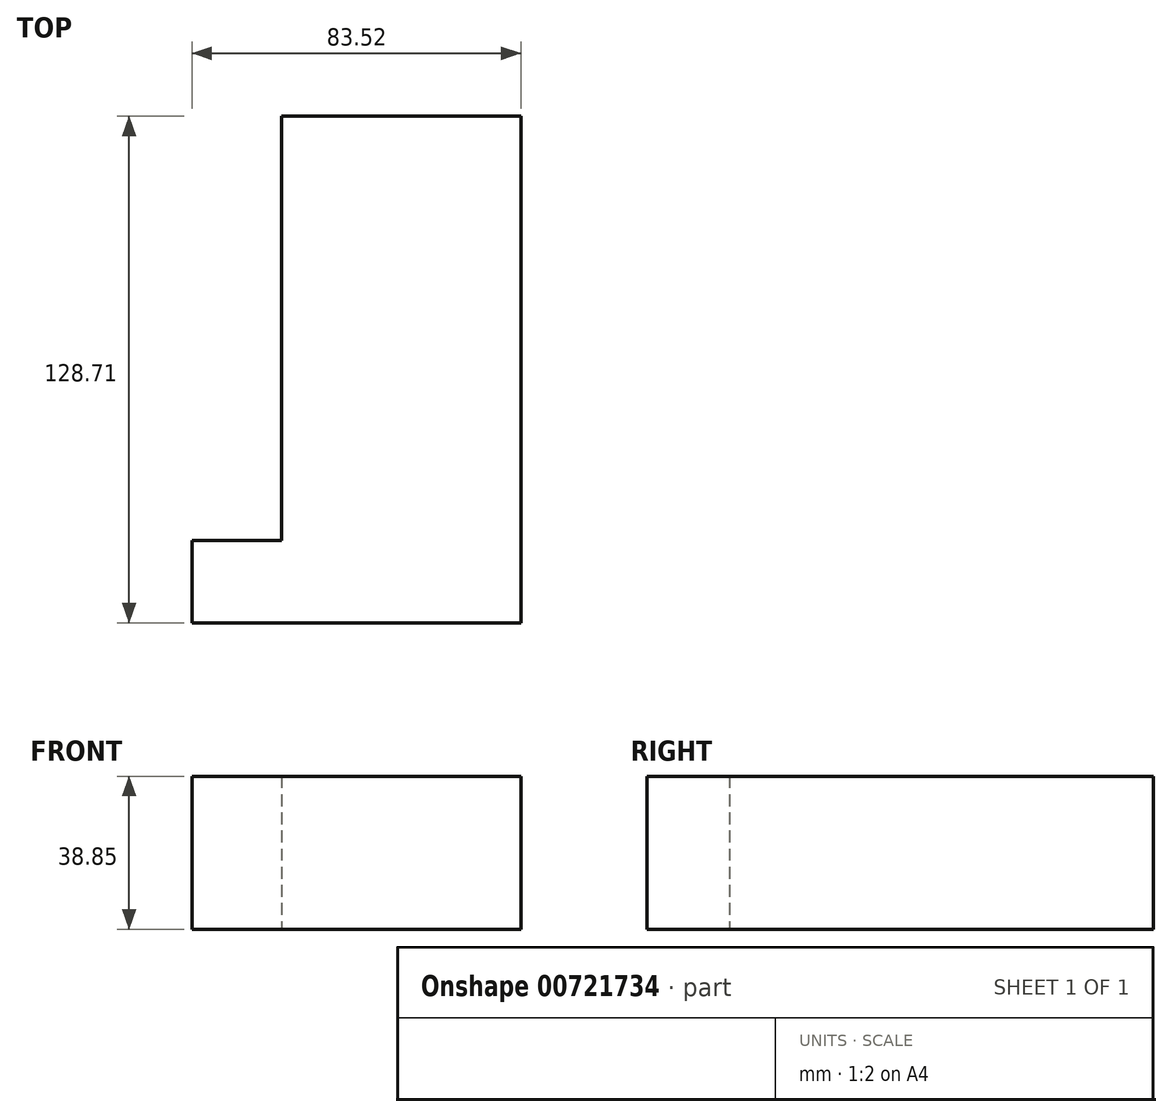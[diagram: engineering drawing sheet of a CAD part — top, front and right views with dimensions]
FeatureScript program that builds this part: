
annotation { "Feature Type Name" : "Feature", "Feature Type Description" : "" }
export const myFeature = defineFeature(function(context is Context, id is Id, definition is map)
    precondition{}
    {
        {
            var Q0;
            Q0=qCreatedBy(makeId("Top.planeOp"),FACE);
            var sketch = newSketch(context, id + "F0", { "sketchPlane" : qUnion([Q0])});
            skLineSegment(sketch, "E0.bottom", {"start": v(-20.99, -41.67) * mm, "end": v(39.74, -41.67) * mm});
            skLineSegment(sketch, "E0.top", {"start": v(-20.99, 66.05) * mm, "end": v(39.74, 66.05) * mm});
            skLineSegment(sketch, "E0.left", {"start": v(-20.99, -41.67) * mm, "end": v(-20.99, 66.05) * mm});
            skLineSegment(sketch, "E0.right", {"start": v(39.74, -41.67) * mm, "end": v(39.74, 66.05) * mm});
            skLineSegment(sketch, "E1.bottom", {"start": v(-43.78, -62.66) * mm, "end": v(-20.99, -62.66) * mm});
            skLineSegment(sketch, "E1.top", {"start": v(-43.78, -41.67) * mm, "end": v(-20.99, -41.67) * mm});
            skLineSegment(sketch, "E1.left", {"start": v(-43.78, -62.66) * mm, "end": v(-43.78, -41.67) * mm});
            skLineSegment(sketch, "E1.right", {"start": v(-20.99, -62.66) * mm, "end": v(-20.99, -41.67) * mm});
            skLineSegment(sketch, "E2.bottom", {"start": v(39.74, -41.67) * mm, "end": v(-43.78, -41.67) * mm});
            skLineSegment(sketch, "E2.top", {"start": v(39.74, -62.66) * mm, "end": v(-43.78, -62.66) * mm});
            skLineSegment(sketch, "E2.left", {"start": v(39.74, -41.67) * mm, "end": v(39.74, -62.66) * mm});
            skLineSegment(sketch, "E2.right", {"start": v(-43.78, -41.67) * mm, "end": v(-43.78, -62.66) * mm});
            skSolve(sketch);
        }
        {
            var Q0;
            {var subQ0=makeQuery(id+"F0.imprint","IMPRINT",EDGE,{"derivedFrom":sQuery(id+"F0.wireOp",EDGE,"E0.bottom")});Q0=qUnion([makeQuery(id+"F0.imprint","IMPRINT",FACE,{"disambiguationData":[TD([[subQ0,1.0]])]}),makeQuery(id+"F0.imprint","IMPRINT",FACE,{"disambiguationData":[TD([[makeQuery(id+"F0.imprint","IMPRINT",EDGE,{"derivedFrom":sQuery(id+"F0.wireOp",EDGE,"E1.bottom")}),1.0]])]}),makeQuery(id+"F0.imprint","IMPRINT",FACE,{"disambiguationData":[TD([[subQ0,-1.0]])]})]);}
            extrude(context, id + "F1", {"entities" : qUnion([Q0]), "depth" : 38.85 * mm, "offsetDistance" : 25.4 * mm});
        }
        {
            var Q0;
            Q0=makeQuery(id+"F1.opExtrude","SWEPT_FACE",FACE,{"disambiguationData":[OSD([sQuery(id+"F0.wireOp",EDGE,"E1.left")])]});
            extrude(context, id + "F2", {"entities" : qUnion([Q0]), "operationType" : NewBodyOperationType.ADD, "oppositeDirection" : true, "depth" : 27.4 * mm, "offsetDistance" : 25.4 * mm});
        }
        {
            var Q0;
            Q0=makeQuery(id+"F1.opExtrude","SWEPT_FACE",FACE,{"disambiguationData":[OSD([sQuery(id+"F0.wireOp",EDGE,"E1.left")])]});
            var sketch = newSketch(context, id + "F3", { "sketchPlane" : qUnion([Q0])});
            skSolve(sketch);
        }
        {
            var Q0;
            {var subQ0=sQuery(id+"F0.wireOp",EDGE,"E1.left");Q0=makeQuery(id+"F3.imprint","IMPRINT",FACE,{"disambiguationData":[TD([[makeQuery(id+"F3.imprint","IMPRINT",EDGE,{"derivedFrom":makeQuery(id+"F1.opExtrude","CAP_EDGE",EDGE,{"disambiguationData":[OSD([subQ0])],"isStart":true})}),-1.0]])]});}
            extrude(context, id + "F4", {"entities" : qUnion([Q0]), "operationType" : NewBodyOperationType.ADD, "oppositeDirection" : true, "depth" : 31.74 * mm, "offsetDistance" : 25.4 * mm});
        }
    });
